# Revit family: Nuaire_IfcFanType_Iaq-Purge2
name_source: partatom
category: Mechanical Equipment
revit_build: Autodesk Revit 2018 (Build: 20170223_1515(x64)
units: mm (PartAtom-declared; Revit-internal decimal feet)

## family parameters
Always vertical = Yes
Cut with Voids When Loaded = No
OmniClass Number = 23.75.00.00
OmniClass Title = Climate Control (HVAC)
Part Type = Normal
Room Calculation Point = No
Round Connector Dimension = Use Radius
Shared = No
Work Plane-Based = No

## types (1)
- Nuaire_IfcFanType_Iaq-Purge2
    6 Monthly = SFG20 20-03
    Annually = SFG20 20-03
    Apparent Load = 195.50 VA
    BMS Links = No
    Battery Supply = No
    Bespoke Timeframe = SFG20 20-03
    CE Approval = Yes
    COBie.Type = Yes
    COBie.Type.Area = 0 m²
    COBie.Type.Category = Pr_65_67_29_12 : Centrifugal fans
    COBie.Type.Description = Inline Purge Fan
    COBie.Type.DurationUnit = Year
    COBie.Type.Length = 560 mm  [stored 1.83727 ft]
    COBie.Type.Manufacturer = Nuaire
    COBie.Type.ModelNumber = IAQ-PURGE
    COBie.Type.ModelReference = IAQ-PURGE
    COBie.Type.Name = IAQ-PURGE
    COBie.Type.NominalHeight = 149 mm  [stored 0.488845 ft]
    COBie.Type.NominalLength = 560 mm  [stored 1.83727 ft]
    COBie.Type.NominalWidth = 299 mm  [stored 0.980971 ft]
    COBie.Type.ReplacementCost = 0 $
    COBie.Type.WarrantyDescription = 2 years parts and labour
    COBie.Type.WarrantyDurationLabor = 2
    COBie.Type.WarrantyDurationParts = 2
    COBie.Type.WarrantyDurationUnit = Year
    COBie.Type.WarrantyGuarantorLabor = Nuaire
    COBie.Type.WarrantyGuarantorParts = Nuaire
    Catalogue Pages = https://www.nuaire.co.uk
    Classification.Uniclass.Pr.Description = Centrifugal fans
    Classification.Uniclass.Pr.Number = Pr_65_67_29_12
    Coverage Area = 0 m²
    Daily = SFG20 20-03
    Description = Inline Purge Fan
    Electrical Phase = 1
    Enclosure Rating = Not rated
    Environmental Product Declaration = WEEE, RoHS
    Fax Number = +44(0)2920-858-222
    Fire Control Panel Links = No
    Full Load Current = 0.85 A
    Height = 149 mm  [stored 0.488845 ft]
    I&M Manual = https://www.nuaire.co.uk
    IFCExportAs = IfcFanType
    IFCExportType = CENTRIFUGALBACKWARDINCLINEDCURVED
    Length = 560 mm  [stored 1.83727 ft]
    Life Cycle Analysis = 0
    Location of Manufacturer = 51.571856, -3.232638
    Maintenance Required 0 to 300hrs = https://www.nuaire.co.uk
    Maintenance Required 1001 to 2000hrs = https://www.nuaire.co.uk
    Maintenance Required 2001 to 4000hrs = https://www.nuaire.co.uk
    Maintenance Required 301 to 600hrs = https://www.nuaire.co.uk
    Maintenance Required 4001 to 8000hrs = https://www.nuaire.co.uk
    Maintenance Required 601 to 1000hrs = https://www.nuaire.co.uk
    Maintenance Required 8001 to 12000hrs = https://www.nuaire.co.uk
    Manufacturer = Nuaire
    Maximum Ambient Temperature = 50 °C
    Model = IAQ-PURGE
    Monthly = SFG20 20-03
    Number of Connection Poles = 2
    OmniClass Number = 23-33 31 19 13
    OmniClass Title = Centrifugal Fans
    Operation and Maintenance Manual = https://www.nuaire.co.uk
    Postcode = CF83 1NA
    Power Source = Mains
    Product Literature = https://www.nuaire.co.uk
    Product Range = MEV
    Quarterly = SFG20 20-03
    Reference Standard = ISO9001:2015
    Responsible Sourcing of Materials = FSC
    Revit Family Last Revised = 2024-05-29T15:45:00
    Spigot Height = 90 mm  [stored 0.295276 ft]
    Spigot Width = 220 mm  [stored 0.721785 ft]
    Telephone Number = +44(0)2920-858-200
    Type Comments = 1
    URL = http://www.nuaire.co.uk
    VAT Registration Number = 877308
    Voltage = 230.00 V
    Warranty Period = 2 years parts and labour
    Weatherproof or Internal Only = Internal
    Weekly = SFG20 20-03
    Weight = 7.00 kg
    Width = 299 mm  [stored 0.980971 ft]

note: [stored X ft] marks values corroborated as IEEE doubles in the binary element streams (Revit-internal decimal feet)

## geometry (parser evidence)
native form markers: Blend x8, Sweep x4
no freeform markers — native parametric forms only
